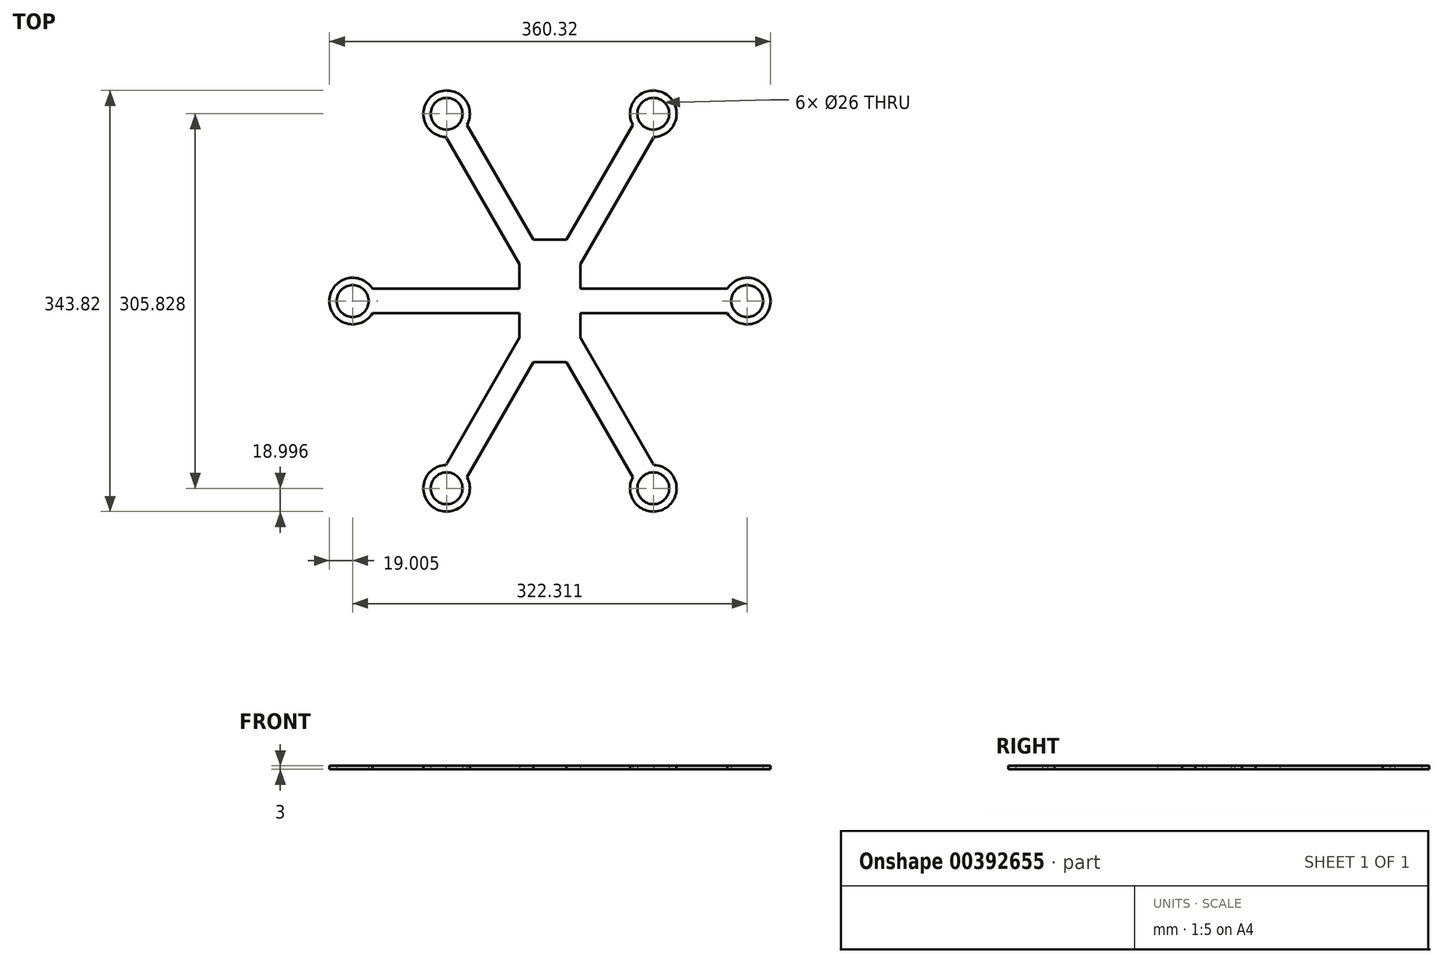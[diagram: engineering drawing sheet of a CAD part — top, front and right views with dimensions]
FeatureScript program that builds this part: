
annotation { "Feature Type Name" : "Feature", "Feature Type Description" : "" }
export const myFeature = defineFeature(function(context is Context, id is Id, definition is map)
    precondition{}
    {
        {
            var Q0;
            Q0=qCreatedBy(makeId("Top.planeOp"),FACE);
            var sketch = newSketch(context, id + "F0", { "sketchPlane" : qUnion([Q0])});
            skLineSegment(sketch, "E0.bottom", {"start": v(25, 50) * mm, "end": v(-25, 50) * mm});
            skLineSegment(sketch, "E0.top", {"start": v(25, -50) * mm, "end": v(-25, -50) * mm});
            skLineSegment(sketch, "E0.left", {"start": v(25, 50) * mm, "end": v(25, -50) * mm});
            skLineSegment(sketch, "E0.right", {"start": v(-25, 50) * mm, "end": v(-25, -50) * mm});
            skPoint(sketch, "E0.middle", {"position": v(0, 0) * mm});
            skLineSegment(sketch, "E1", {"start": v(25, 10) * mm, "end": v(145, 10) * mm});
            skLineSegment(sketch, "E2", {"start": v(145, -10) * mm, "end": v(25, -10) * mm});
            skLineSegment(sketch, "E3", {"start": v(25, 30) * mm, "end": v(85, 133.92) * mm});
            skLineSegment(sketch, "E4", {"start": v(67.68, 143.92) * mm, "end": v(13.45, 50) * mm});
            skLineSegment(sketch, "E5", {"start": v(-13.45, 50) * mm, "end": v(-67.68, 143.92) * mm});
            skLineSegment(sketch, "E6", {"start": v(-85, 133.92) * mm, "end": v(-25, 30) * mm});
            skLineSegment(sketch, "E7", {"start": v(-25, 10) * mm, "end": v(-145, 10) * mm});
            skLineSegment(sketch, "E8", {"start": v(-145, -10) * mm, "end": v(-25, -10) * mm});
            skLineSegment(sketch, "E9", {"start": v(-25, -30) * mm, "end": v(-85, -133.92) * mm});
            skLineSegment(sketch, "E10", {"start": v(-67.68, -143.92) * mm, "end": v(-13.45, -50) * mm});
            skLineSegment(sketch, "E11", {"start": v(13.45, -50) * mm, "end": v(67.68, -143.92) * mm});
            skLineSegment(sketch, "E12", {"start": v(85, -133.92) * mm, "end": v(25, -30) * mm});
            skCircle(sketch, "E13", {"center": v(-161.16, 0) * mm, "radius": 19 * mm});
            skCircle(sketch, "E14", {"center": v(-161.16, 0) * mm, "radius": 13 * mm});
            skCircle(sketch, "E15", {"center": v(161.16, 0) * mm, "radius": 19 * mm});
            skCircle(sketch, "E16", {"center": v(161.16, 0) * mm, "radius": 13 * mm});
            skCircle(sketch, "E17", {"center": v(84.42, 152.91) * mm, "radius": 19 * mm});
            skCircle(sketch, "E18", {"center": v(84.42, 152.91) * mm, "radius": 13 * mm});
            skCircle(sketch, "E19", {"center": v(-84.42, 152.91) * mm, "radius": 19 * mm});
            skCircle(sketch, "E20", {"center": v(-84.42, 152.91) * mm, "radius": 13 * mm});
            skCircle(sketch, "E21", {"center": v(-84.42, -152.91) * mm, "radius": 19 * mm});
            skCircle(sketch, "E22", {"center": v(-84.42, -152.91) * mm, "radius": 13 * mm});
            skCircle(sketch, "E23", {"center": v(84.42, -152.91) * mm, "radius": 19 * mm});
            skCircle(sketch, "E24", {"center": v(84.42, -152.91) * mm, "radius": 13 * mm});
            skSolve(sketch);
        }
        {
            var Q0;
            Q0 = qSketchRegion(id + "F0", true);
            extrude(context, id + "F1", {"entities" : qUnion([Q0]), "depth" : 3 * mm});
        }
    });
